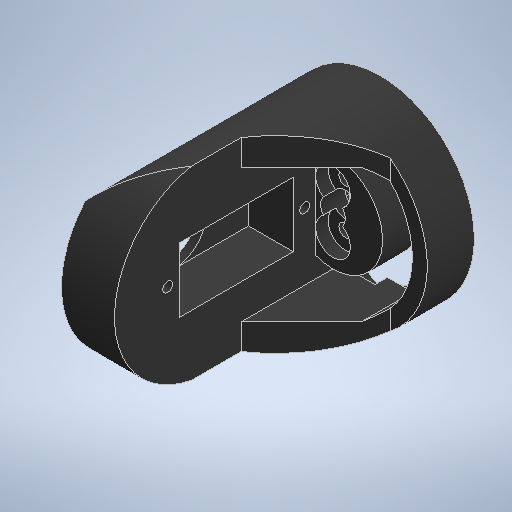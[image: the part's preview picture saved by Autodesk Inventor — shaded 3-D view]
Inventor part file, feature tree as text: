
AUTODESK INVENTOR PART (.ipt)
format: ipt  version: 2025.2 (Build 292293000, 293)  size: 408,064 bytes
history: native  units: mm
features: extrude x13, sketch x11, mirror x2, chamfer x1, projected_geometry x1
ambient origin geometry x8: Origin, YZ Plane, XZ Plane, XY Plane, X Axis, Y Axis, Z Axis, Center Point
bodies: Body1 (feature_tree)
feature tree (28):
  extrude  "Extrusion28"  Depth=38.0mm
  extrude  "Extrusion34"  Depth=40.5mm
  extrude  "Extrusion35"  Depth=38.0mm
  sketch  "Sketch36"  dims[d258=28.0mm d259=0.0mm d260=0.0mm]
  extrude  "Extrusion36"  TaperAngle=0.0deg  [1 undecoded]
  extrude  "Extrusion37"  Depth=13.0mm
  sketch  "Sketch38"  dims[d261=13.0mm d262=8.0mm]
  extrude  "Extrusion40"  Depth=10.0mm TaperAngle=0.0deg
  extrude  "Extrusion41"  Depth=2.0mm
  extrude  "Extrusion42"  Depth=10.7mm
  extrude  "Extrusion43"  Depth=23.0mm
  extrude  "Extrusion44"  Depth=9.0mm TaperAngle=0.0deg
  mirror  "Mirror2"
  extrude  "Extrusion45"  Depth=2.5mm
  mirror  "Mirror3"
  extrude  "Extrusion46"  Depth=2.5mm
  chamfer  "Chamfer4"  Distance=2.0mm
  extrude  "Extrusion47"  TaperAngle=0.0deg  [1 undecoded]
  sketch  "Sketch30"  dims[d237=50.0mm d238=0.0mm d252=38.0mm]
  sketch  "Sketch33"  dims[d253=14.2mm d254=40.5mm]
  sketch  "Sketch35"  dims[d255=50.0mm d256=0.0mm d257=38.0mm]
  projected_geometry  "Projected Loop6"
  sketch  "Sketch39"  dims[d265=6.5mm d266=10.0mm d267=0.0mm]
  sketch  "Sketch40"  dims[d268=2.0mm d269=0.0mm d271=2.0mm]
  sketch  "Sketch41"  dims[d272=9.0mm d277=10.7mm]
  sketch  "Sketch42"  dims[d278=2.0mm d281=23.0mm]
  sketch  "Sketch43"  dims[d282=13.0mm d284=9.0mm d285=0.0mm]
  sketch  "Sketch44"  dims[d286=2.0mm d287=2.3mm d288=2.3mm d289=2.0mm d290=0.0mm d291=0.0mm d292=32.0mm d293=2.0mm d294=0.0mm d295=20.0mm d296=3.5mm d297=27.0mm d298=0.0mm d299=0.0mm d300=7.0mm d301=14.0mm d302=4.5mm d303=0.0mm d305=10.0mm d306=7.5mm d307=5.5mm d308=2.5mm d309=0.0mm d310=5.0mm d311=2.6mm d312=9.0mm d313=2.5mm d314=0.0mm d315=15.0mm d316=2.0mm d317=45.0deg d318=7.0mm d319=2.5mm d320=0.0mm]
note: 2 required parameter values undecoded (feature->parameter linkage not recoverable at this tier; creation-order binding heuristic only, values carry confidence <= 0.55)
